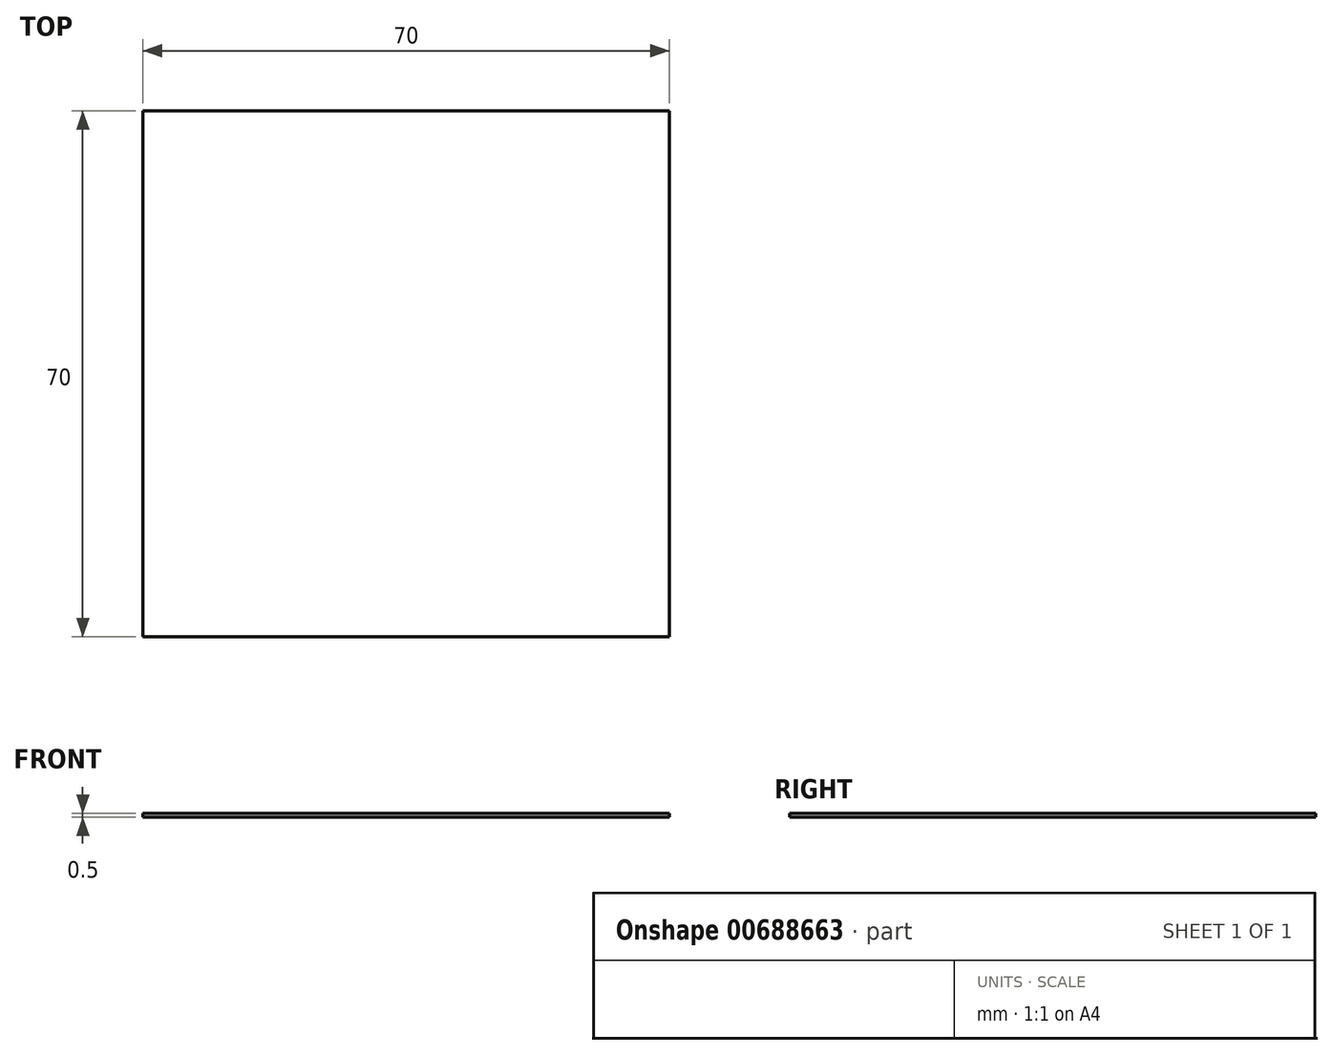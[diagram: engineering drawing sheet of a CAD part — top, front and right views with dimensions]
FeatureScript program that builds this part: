
annotation { "Feature Type Name" : "Feature", "Feature Type Description" : "" }
export const myFeature = defineFeature(function(context is Context, id is Id, definition is map)
    precondition{}
    {
        {
            var Q0;
            Q0=qCreatedBy(makeId("Top.planeOp"),FACE);
            var sketch = newSketch(context, id + "F0", { "sketchPlane" : qUnion([Q0])});
            skLineSegment(sketch, "E0.bottom", {"start": v(-102.5, -28.43) * mm, "end": v(-32.5, -28.43) * mm});
            skLineSegment(sketch, "E0.top", {"start": v(-102.5, -98.43) * mm, "end": v(-32.5, -98.43) * mm});
            skLineSegment(sketch, "E0.left", {"start": v(-102.5, -28.43) * mm, "end": v(-102.5, -98.43) * mm});
            skLineSegment(sketch, "E0.right", {"start": v(-32.5, -28.43) * mm, "end": v(-32.5, -98.43) * mm});
            skSolve(sketch);
        }
        {
            var Q0;
            Q0=makeQuery(id+"F0.imprint","IMPRINT",FACE,{"disambiguationData":[TD([[makeQuery(id+"F0.imprint","IMPRINT",EDGE,{"derivedFrom":sQuery(id+"F0.wireOp",EDGE,"E0.bottom")}),-1.0]])]});
            var Q1;
            Q1=sQuery(id+"F0.wireOp",EDGE,"E0.right");
            var Q2;
            Q2=sQuery(id+"F0.wireOp",EDGE,"E0.top");
            var Q3;
            Q3=sQuery(id+"F0.wireOp",EDGE,"E0.left");
            var Q4;
            Q4=sQuery(id+"F0.wireOp",EDGE,"E0.bottom");
            extrude(context, id + "F1", {"entities" : qUnion([Q0]), "surfaceEntities" : qUnion([Q1, Q2, Q3, Q4]), "depth" : .5 * mm, "offsetDistance" : 25 * mm});
        }
    });
